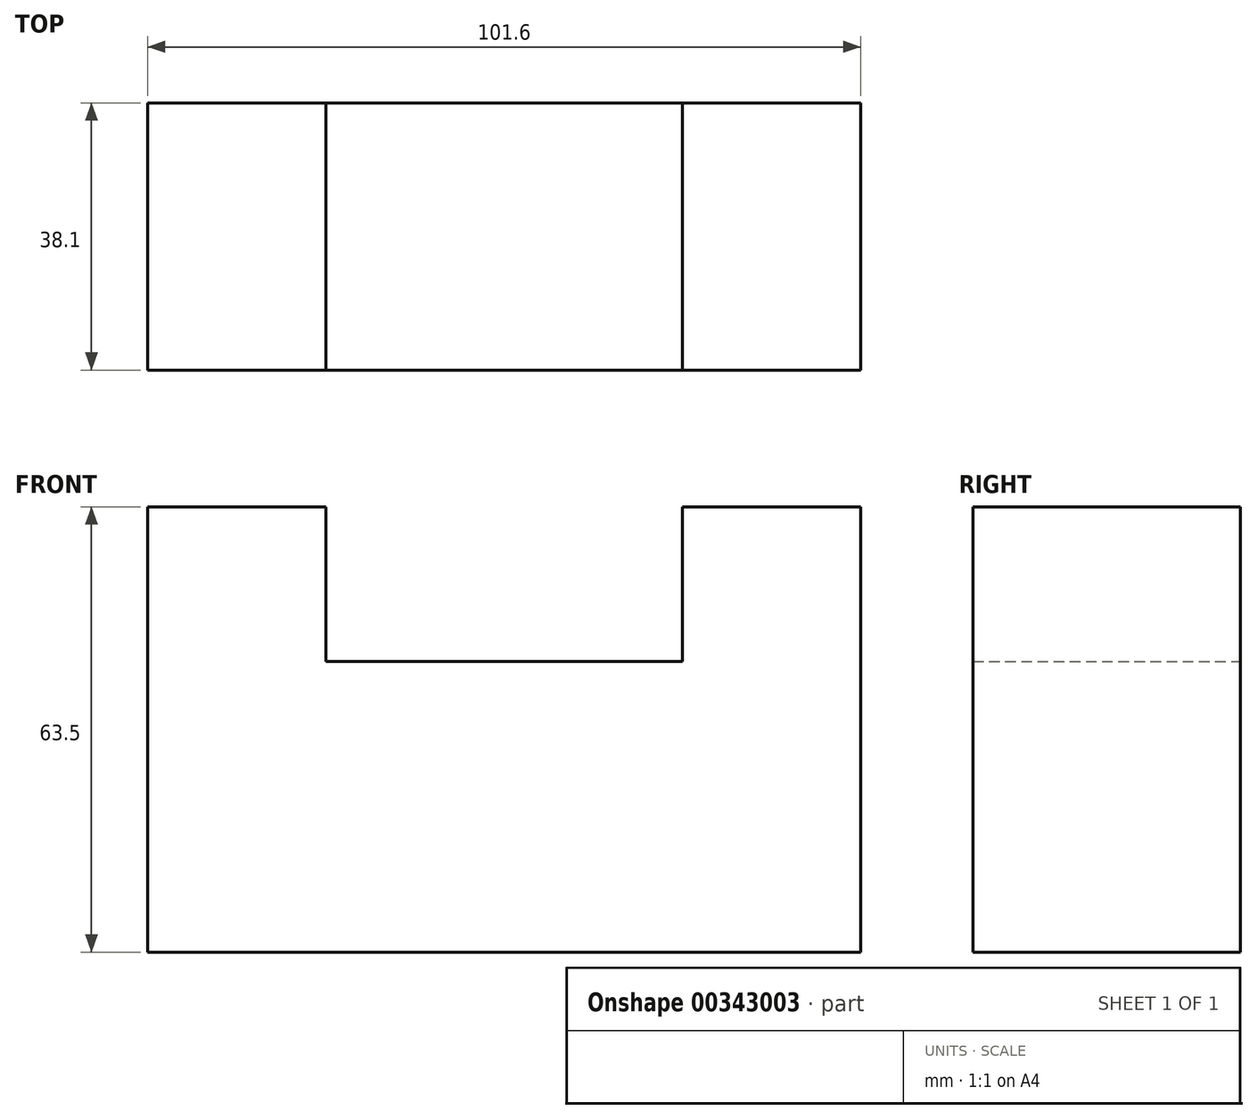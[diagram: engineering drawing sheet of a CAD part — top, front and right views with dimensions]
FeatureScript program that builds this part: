
annotation { "Feature Type Name" : "Feature", "Feature Type Description" : "" }
export const myFeature = defineFeature(function(context is Context, id is Id, definition is map)
    precondition{}
    {
        {
            var Q0;
            Q0=qCreatedBy(makeId("Front.planeOp"),FACE);
            var sketch = newSketch(context, id + "F0", { "sketchPlane" : qUnion([Q0])});
            skLineSegment(sketch, "E0", {"start": v(-58.83, 45.43) * mm, "end": v(-58.83, -18.07) * mm});
            skLineSegment(sketch, "E1", {"start": v(-58.83, -18.07) * mm, "end": v(42.77, -18.07) * mm});
            skLineSegment(sketch, "E2", {"start": v(42.77, -18.07) * mm, "end": v(42.77, 45.43) * mm});
            skLineSegment(sketch, "E3", {"start": v(42.77, 45.43) * mm, "end": v(17.37, 45.43) * mm});
            skLineSegment(sketch, "E4", {"start": v(17.37, 23.38) * mm, "end": v(17.37, 45.43) * mm});
            skLineSegment(sketch, "E5", {"start": v(17.37, 23.38) * mm, "end": v(-33.43, 23.38) * mm});
            skLineSegment(sketch, "E6", {"start": v(-33.43, 23.38) * mm, "end": v(-33.43, 45.43) * mm});
            skLineSegment(sketch, "E7", {"start": v(-33.43, 45.43) * mm, "end": v(-58.83, 45.43) * mm});
            skSolve(sketch);
        }
        {
            var Q0;
            Q0 = qSketchRegion(id + "F0", true);
            extrude(context, id + "F1", {"entities" : qUnion([Q0]), "depth" : 38.1 * mm});
        }
    });
